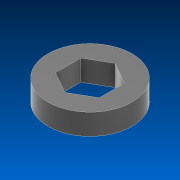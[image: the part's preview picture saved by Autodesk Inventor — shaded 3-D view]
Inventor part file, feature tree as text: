
AUTODESK INVENTOR PART (.ipt)
format: ipt  version: 2022 (Build 260153000, 153)  size: 93,184 bytes
history: native  units: in
note: dims shown in document units (in); Inventor stores cm internally (conversion verified against a paired STEP export)
features: extrude x1, sketch x1
ambient origin geometry x8: Origin, YZ Plane, XZ Plane, XY Plane, X Axis, Y Axis, Z Axis, Center Point
bodies: Solid1 (feature_tree)
feature tree (2):
  extrude  "Extrusion1"  Depth=0.125in
  sketch  "Sketch1"  dims[d0=0.26in d1=0.5in d2=0.125in d3=0.0in]
